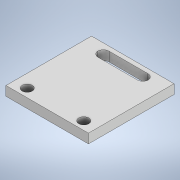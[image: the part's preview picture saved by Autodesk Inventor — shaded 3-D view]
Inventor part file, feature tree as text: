
AUTODESK INVENTOR PART (.ipt)
format: ipt  version: 2020 (Build 240168000, 168)  size: 123,904 bytes
history: native  units: in
note: dims shown in document units (in); Inventor stores cm internally (conversion verified against a paired STEP export)
features: extrude x2, sketch x2, fillet x1
ambient origin geometry x8: Origin, YZ Plane, XZ Plane, XY Plane, X Axis, Y Axis, Z Axis, Center Point
bodies: Solid1 (feature_tree)
feature tree (5):
  extrude  "Extrusion1"  Depth=1.188in
  extrude  "Extrusion2"  Depth=0.08in
  fillet  "Fillet1"  Radius=0.14in
  sketch  "Sketch1"  dims[d0=1.145in d1=1.188in]
  sketch  "Sketch2"  dims[d2=0.13in d3=0.0in d4=0.14in d5=0.14in d6=0.785in d7=0.115in d8=0.06in d9=0.15in d10=0.7in d11=0.0in d12=0.0in d13=0.08in]
